# Revit family: Basin-Undercounter-DXV-Webster-D00426000.415
name_source: partatom
category: Plumbing Fixtures
revit_build: Autodesk Revit 2014 (Build: 20130308_1515(x64)
units: mm (PartAtom-declared; Revit-internal decimal feet)

## types (1)
- D00426000.415
    ADA Compliant = Yes
    Assembly Code = D2010310
    Basin Shape = Square
    CW Connection = Yes
    CWFU = 1.5
    Cold Water Connection Diameter = 1/2"
    Cold Water Connection Height = 11"
    Cold Water Connection Radius = 1/4"
    Cold Water Connection Width = 4"
    Connection Location = 3 1/2"
    Default Elevation = 0"
    Description = Webster Square Under Counter Lavatory
    Finish = Vitreous China-DXV-415-Canvas White
    HW Connection = Yes
    HWFU = 1.5
    Height = 6 3/4"
    Hot Water Connection Diameter = 1/2"
    Hot Water Connection Height = 11"
    Hot Water Connection Radius = 1/4"
    Hot Water Connection Width = 4"
    Installation Type = Undercounter
    Length = 16"
    Manufacturer = DXV
    Material = Vitreous China-DXV-415-Canvas White
    Model = D00426000.415
    Product Documentation Link = https://dxv01.blob.core.windows.net
    Product Page URL = https://www.dxv.com
    Revised Date = 11/29/2017
    URL = https://www.dxv.com
    Vent Connection = No
    WFU = 2
    Warranty Documentation Link = https://www.dxv.com
    Waste Connection = Yes
    Waste Connection Diameter = 1 1/4"
    Waste Connection Height = 13"
    Waste Connection Radius = 5/8"
    Width = 16"

## geometry (parser evidence)
native form markers: Sweep x1
no freeform markers — native parametric forms only
